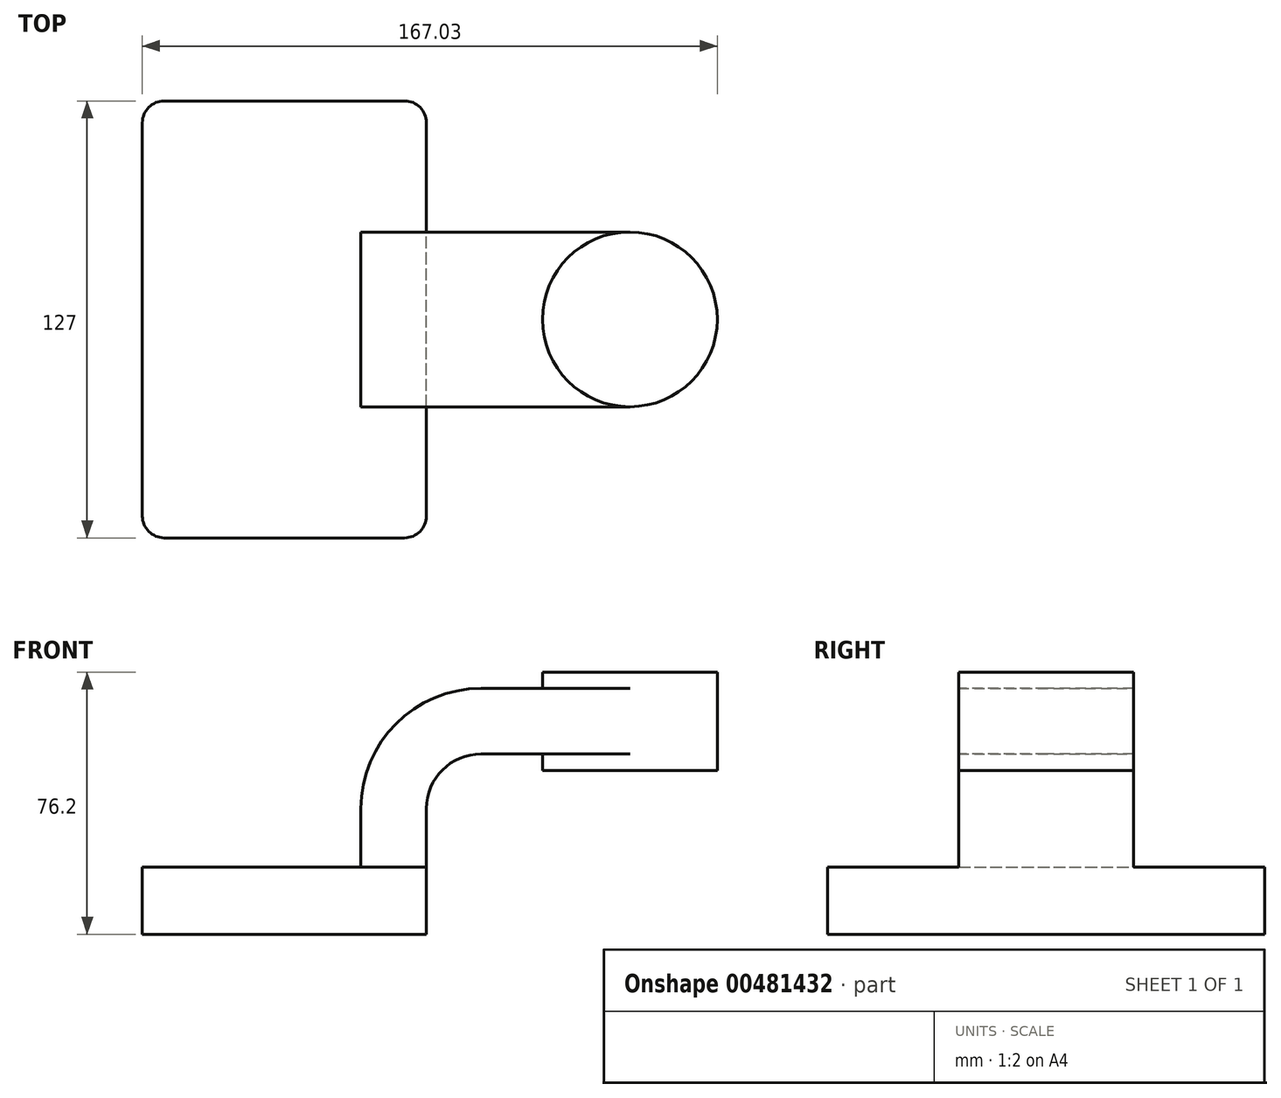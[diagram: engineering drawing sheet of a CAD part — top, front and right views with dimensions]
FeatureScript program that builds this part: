
annotation { "Feature Type Name" : "Feature", "Feature Type Description" : "" }
export const myFeature = defineFeature(function(context is Context, id is Id, definition is map)
    precondition{}
    {
        {
            var Q0;
            Q0=qCreatedBy(makeId("Front.planeOp"),FACE);
            var sketch = newSketch(context, id + "F0", { "sketchPlane" : qUnion([Q0])});
            skLineSegment(sketch, "E0.bottom", {"start": v(-41.28, 9.74) * mm, "end": v(41.28, 9.74) * mm});
            skLineSegment(sketch, "E0.top", {"start": v(-41.28, -9.74) * mm, "end": v(41.28, -9.74) * mm});
            skLineSegment(sketch, "E0.left", {"start": v(-41.28, 9.74) * mm, "end": v(-41.28, -9.74) * mm});
            skLineSegment(sketch, "E0.right", {"start": v(41.28, 9.74) * mm, "end": v(41.28, -9.74) * mm});
            skPoint(sketch, "E0.middle", {"position": v(0, 0) * mm});
            skLineSegment(sketch, "E1.bottom", {"start": v(74.96, 66.46) * mm, "end": v(125.76, 66.46) * mm});
            skLineSegment(sketch, "E1.top", {"start": v(74.96, 37.88) * mm, "end": v(125.76, 37.88) * mm});
            skLineSegment(sketch, "E1.left", {"start": v(74.96, 66.46) * mm, "end": v(74.96, 37.88) * mm});
            skLineSegment(sketch, "E1.right", {"start": v(125.76, 66.46) * mm, "end": v(125.76, 37.88) * mm});
            skPoint(sketch, "E1.middle", {"position": v(100.36, 52.17) * mm});
            skLineSegment(sketch, "E2", {"start": v(41.28, 9.74) * mm, "end": v(41.28, 26.78) * mm});
            skArc(sketch, "E3", {"start": v(41.27, 26.78) * mm, "mid": v(45.92, 38) * mm, "end": v(57.15, 42.66) * mm});
            skLineSegment(sketch, "E4", {"start": v(57.15, 42.66) * mm, "end": v(100.36, 42.66) * mm});
            skLineSegment(sketch, "E5.0", {"start": v(57.15, 61.7) * mm, "end": v(100.36, 61.7) * mm});
            skArc(sketch, "E5.1", {"start": v(22.23, 26.78) * mm, "mid": v(32.45, 51.48) * mm, "end": v(57.15, 61.7) * mm});
            skLineSegment(sketch, "E5.2", {"start": v(22.23, 9.74) * mm, "end": v(22.23, 26.78) * mm});
            skLineSegment(sketch, "E6", {"start": v(100.36, 37.88) * mm, "end": v(100.36, 66.46) * mm});
            skFitSpline(sketch, "E7", {"points": [v(-41.28, 9.74) * mm, v(57.15, 61.7) * mm], "startDerivative": vector(33.25, 82.56) * mm, "endDerivative": vector(151.97, -3.5) * mm});
            skSolve(sketch);
        }
        {
            var Q0;
            Q0=makeQuery(id+"F0.imprint","IMPRINT",FACE,{"disambiguationData":[TD([[makeQuery(id+"F0.imprint","IMPRINT",EDGE,{"derivedFrom":sQuery(id+"F0.wireOp",EDGE,"E0.top")}),1.0]])]});
            extrude(context, id + "F1", {"entities" : qUnion([Q0]), "endBound" : BoundingType.SYMMETRIC, "depth" : 127 * mm});
        }
        {
            var Q0;
            {var subQ1=sQuery(id+"F0.wireOp",EDGE,"E2");Q0=makeQuery(id+"F0.imprint","IMPRINT",FACE,{"disambiguationData":[TD([[makeQuery(id+"F0.imprint","IMPRINT",EDGE,{"derivedFrom":subQ1}),1.0]])]});}
            var Q1;
            {var subQ0=sQuery(id+"F0.wireOp",EDGE,"E5.0");var subQ1=sQuery(id+"F0.wireOp",EDGE,"E1.left");var subQ2=makeQuery(id+"F0.imprint","INTERSECT",VERTEX,{"derivedFrom":[subQ1,subQ0]});Q1=makeQuery(id+"F0.imprint","IMPRINT",FACE,{"disambiguationData":[TD([[makeQuery(id+"F0.imprint","IMPRINT",EDGE,{"disambiguationData":[TD([[subQ2,-1.0]])],"derivedFrom":subQ1}),1.0]])]});}
            extrude(context, id + "F2", {"entities" : qUnion([Q0, Q1]), "endBound" : BoundingType.SYMMETRIC, "depth" : 50.8 * mm});
        }
        {
            var Q0;
            Q0=makeQuery(id+"F0.imprint","IMPRINT",FACE,{"disambiguationData":[TD([[makeQuery(id+"F0.imprint","IMPRINT",EDGE,{"derivedFrom":sQuery(id+"F0.wireOp",EDGE,"E5.1")}),1.0]])]});
            extrude(context, id + "F3", {"entities" : qUnion([Q0]), "operationType" : NewBodyOperationType.ADD, "endBound" : BoundingType.SYMMETRIC, "depth" : 15.88 * mm});
        }
        {
            var Q0;
            {var subQ0=sQuery(id+"F0.wireOp",EDGE,"E1.right");Q0=makeQuery(id+"F0.imprint","IMPRINT",FACE,{"disambiguationData":[TD([[makeQuery(id+"F0.imprint","IMPRINT",EDGE,{"derivedFrom":subQ0}),-1.0]])]});}
            var Q1;
            Q1=sQuery(id+"F0.wireOp",EDGE,"E6");
            revolve(context, id + "F4", {"operationType" : NewBodyOperationType.ADD, "entities" : qUnion([Q0]), "axis" : qUnion([Q1]), "revolveType" : RevolveType.FULL});
        }
        {
            var Q0;
            Q0=makeQuery(id+"F1.opExtrude","CAP_EDGE",EDGE,{"disambiguationData":[OSD([sQuery(id+"F0.wireOp",EDGE,"E0.left")])],"isStart":false});
            var Q1;
            Q1=makeQuery(id+"F1.opExtrude","CAP_EDGE",EDGE,{"disambiguationData":[OSD([sQuery(id+"F0.wireOp",EDGE,"E0.right")])],"isStart":false});
            var Q2;
            Q2=makeQuery(id+"F1.opExtrude","CAP_EDGE",EDGE,{"disambiguationData":[OSD([sQuery(id+"F0.wireOp",EDGE,"E0.right")])],"isStart":true});
            var Q3;
            Q3=makeQuery(id+"F1.opExtrude","CAP_EDGE",EDGE,{"disambiguationData":[OSD([sQuery(id+"F0.wireOp",EDGE,"E0.left")])],"isStart":true});
            fillet(context, id + "F5", {"entities" : qUnion([Q0, Q1, Q2, Q3]), "radius" : 6.35 * mm, "tangentPropagation" : true, "allowEdgeOverflow" : false});
        }
    });
